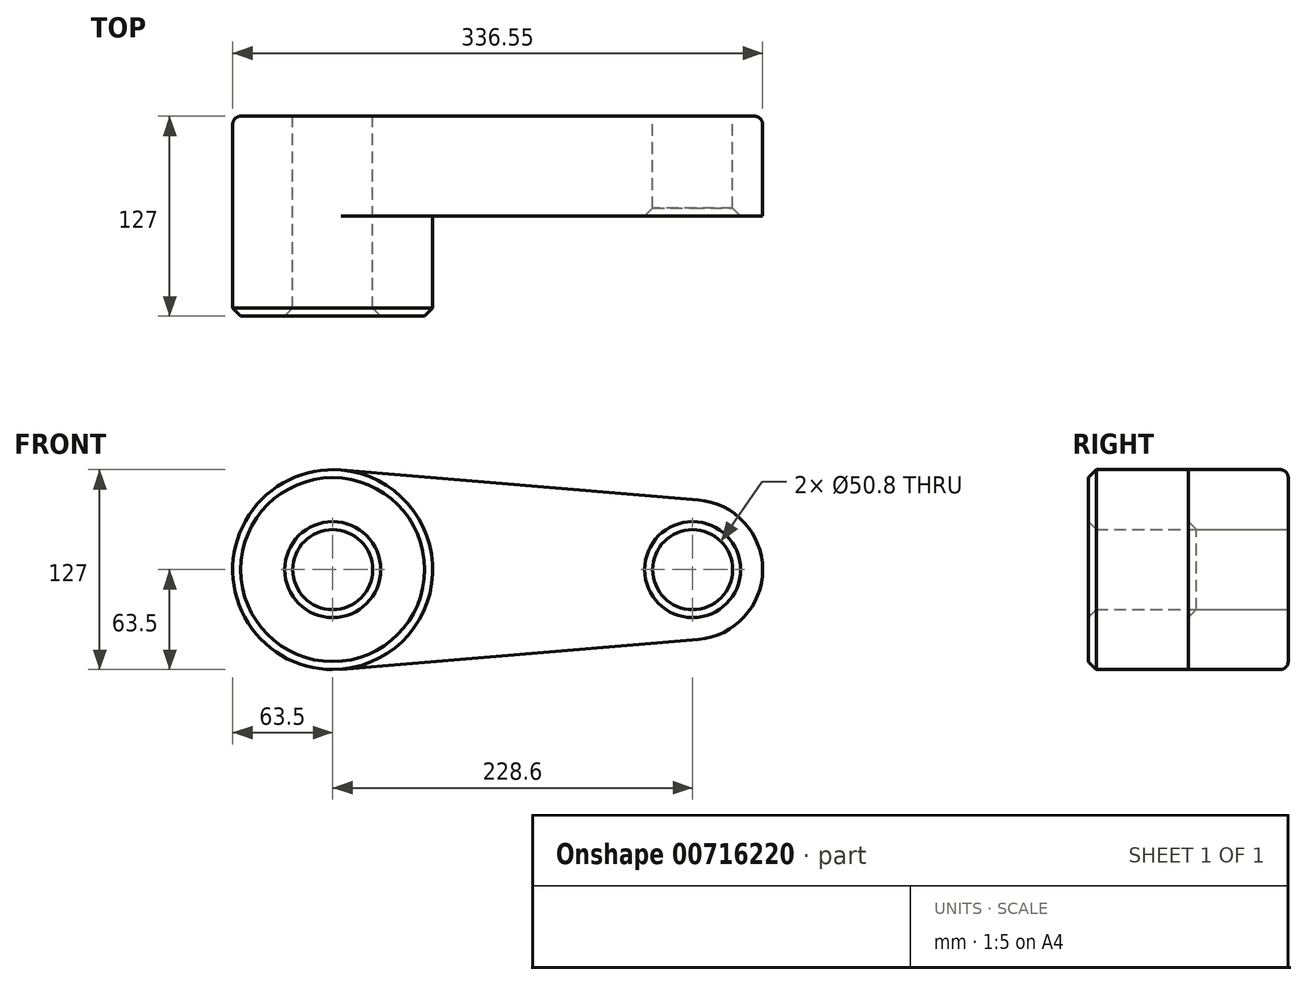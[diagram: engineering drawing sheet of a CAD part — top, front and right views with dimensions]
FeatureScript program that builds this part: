
annotation { "Feature Type Name" : "Feature", "Feature Type Description" : "" }
export const myFeature = defineFeature(function(context is Context, id is Id, definition is map)
    precondition{}
    {
        {
            var Q0;
            Q0=qCreatedBy(makeId("Front.planeOp"),FACE);
            var sketch = newSketch(context, id + "F0", { "sketchPlane" : qUnion([Q0])});
            skCircle(sketch, "E0", {"center": v(0, 0) * mm, "radius": 63.5 * mm});
            skCircle(sketch, "E1", {"center": v(228.6, 0) * mm, "radius": 44.45 * mm});
            skLineSegment(sketch, "E2", {"start": v(5.3, 63.28) * mm, "end": v(232.3, 44.3) * mm});
            skLineSegment(sketch, "E3", {"start": v(5.3, -63.28) * mm, "end": v(232.3, -44.3) * mm});
            skCircle(sketch, "E4", {"center": v(228.6, 0) * mm, "radius": 25.4 * mm});
            skCircle(sketch, "E5", {"center": v(0, 0) * mm, "radius": 25.4 * mm});
            skSolve(sketch);
        }
        {
            var Q0;
            Q0 = qSketchRegion(id + "F0", true);
            extrude(context, id + "F1", {"entities" : qUnion([Q0]), "depth" : 63.5 * mm, "offsetDistance" : 25.4 * mm});
        }
        {
            var Q0;
            Q0=makeQuery(id+"F0.imprint","IMPRINT",FACE,{"disambiguationData":[TD([[makeQuery(id+"F0.imprint","IMPRINT",EDGE,{"derivedFrom":sQuery(id+"F0.wireOp",EDGE,"E5")}),-1.0]])]});
            extrude(context, id + "F2", {"entities" : qUnion([Q0]), "operationType" : NewBodyOperationType.ADD, "depth" : 127 * mm, "offsetDistance" : 25.4 * mm});
        }
        {
            var Q0;
            Q0=makeQuery(id+"F2.opExtrude","CAP_EDGE",EDGE,{"disambiguationData":[OSD([sQuery(id+"F0.wireOp",EDGE,"E5")])],"isStart":false});
            var Q1;
            Q1=makeQuery(id+"F2.opExtrude","CAP_EDGE",EDGE,{"disambiguationData":[OSD([sQuery(id+"F0.wireOp",EDGE,"E0")])],"isStart":false});
            var Q2;
            Q2=makeQuery(id+"F1.opExtrude","CAP_EDGE",EDGE,{"disambiguationData":[OSD([sQuery(id+"F0.wireOp",EDGE,"E4")])],"isStart":false});
            chamfer(context, id + "F3", {"entities" : qUnion([Q0, Q1, Q2]), "width" : 5.08 * mm, "tangentPropagation" : true});
        }
        {
            var Q0;
            Q0=makeQuery(id+"F1.opExtrude","CAP_EDGE",EDGE,{"disambiguationData":[OSD([sQuery(id+"F0.wireOp",EDGE,"E2")])],"isStart":true});
            var Q1;
            Q1=makeQuery(id+"F1.opExtrude","CAP_EDGE",EDGE,{"disambiguationData":[OSD([sQuery(id+"F0.wireOp",EDGE,"E3")])],"isStart":true});
            var Q2;
            Q2=makeQuery(id+"F1.opExtrude","CAP_EDGE",EDGE,{"disambiguationData":[OSD([sQuery(id+"F0.wireOp",EDGE,"E0")])],"isStart":true});
            var Q3;
            Q3=makeQuery(id+"F1.opExtrude","CAP_EDGE",EDGE,{"disambiguationData":[OSD([sQuery(id+"F0.wireOp",EDGE,"E1")])],"isStart":true});
            fillet(context, id + "F4", {"entities" : qUnion([Q0, Q1, Q2, Q3]), "radius" : 5.08 * mm, "tangentPropagation" : true, "allowEdgeOverflow" : false});
        }
    });
